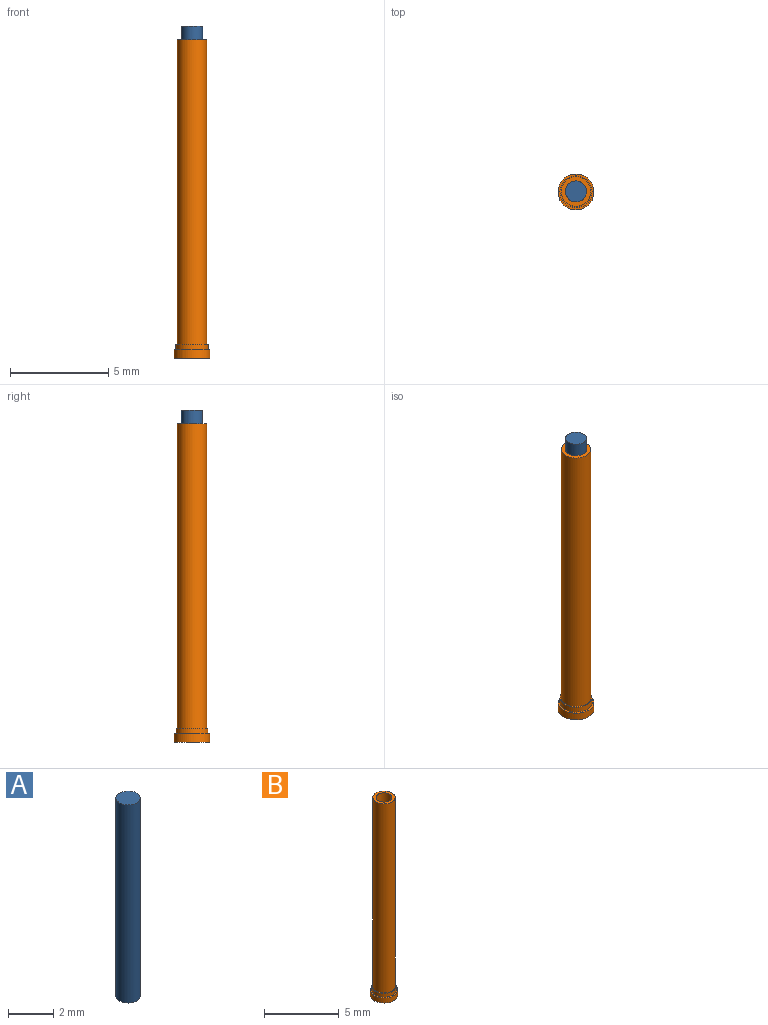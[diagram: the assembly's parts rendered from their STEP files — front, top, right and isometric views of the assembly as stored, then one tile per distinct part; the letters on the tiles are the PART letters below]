
ASSEMBLY  parts=2 mates=1
PART A: 3 faces, bbox 1.1x1.1x10.7 mm
  f0: cylinder r=0.54mm len=10.7mm, axis (0,0,-1), area 36mm2, adj f1,f2
  f1: plane 1.07x1.07mm, normal (0,0,1), area 0.9mm2, adj f0
  f2: plane 1.07x1.07mm, normal (0,0,-1), area 0.9mm2, adj f0
PART B: 9 faces, bbox 1.8x1.8x16.2 mm
  f0: cylinder r=0.92mm len=1.83mm, axis (0,0,-1), area 2.4mm2, adj f1,f2
  f1: plane 1.83x1.83mm, normal (0,0,1), area 0.5mm2, adj f0,f3
  f2: plane 1.83x1.83mm, normal (0,0,-1), area 2.6mm2, adj f0
  f3: cylinder r=0.81mm len=1.63mm, axis (0,0,-1), area 1.5mm2, adj f1,f4
  f4: plane 1.63x1.63mm, normal (0,0,1), area 0.3mm2, adj f3,f6
  f5: plane 1.5x1.5mm, normal (0,0,1), area 0.9mm2, adj f6,f7
  f6: cylinder r=0.75mm len=15.49mm, axis (0,0,-1), area 73mm2, adj f4,f5
  f7: cylinder r=0.54mm len=10mm, axis (0,0,1), area 33.6mm2, adj f5,f8
  f8: plane 1.07x1.07mm, normal (0,0,1), area 0.9mm2, adj f7
PLACE A t=(0.44,7.04,2.13)mm
PLACE B rot(axis=(0,0,-1),90deg) t=(0.44,7.04,-4.07)mm
MATE slider B.f7 <-> A.f0  axis (0,0,1) through (0.44,7.04,2.13)mm
